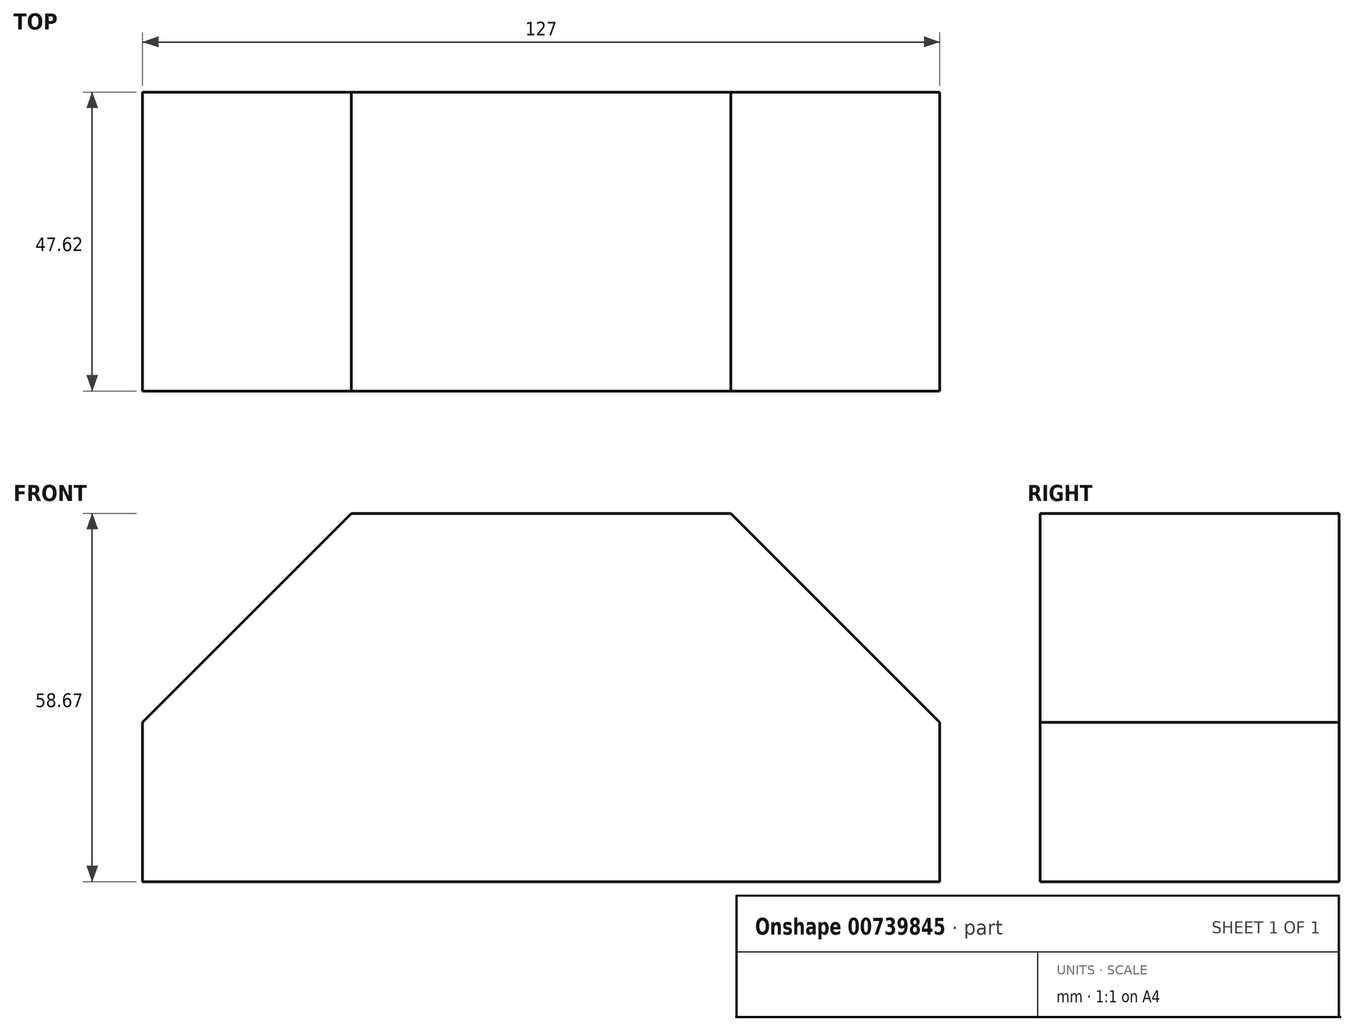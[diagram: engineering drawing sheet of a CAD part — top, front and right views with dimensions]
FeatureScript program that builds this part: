
annotation { "Feature Type Name" : "Feature", "Feature Type Description" : "" }
export const myFeature = defineFeature(function(context is Context, id is Id, definition is map)
    precondition{}
    {
        {
            var Q0;
            Q0=qCreatedBy(makeId("Front.planeOp"),FACE);
            var sketch = newSketch(context, id + "F0", { "sketchPlane" : qUnion([Q0])});
            skLineSegment(sketch, "E0", {"start": v(-62.45, -58.67) * mm, "end": v(64.55, -58.67) * mm});
            skLineSegment(sketch, "E1", {"start": v(64.55, -58.67) * mm, "end": v(64.55, -33.27) * mm});
            skLineSegment(sketch, "E2", {"start": v(64.55, -33.27) * mm, "end": v(31.27, 0) * mm});
            skLineSegment(sketch, "E3", {"start": v(31.27, 0) * mm, "end": v(-29.18, 0) * mm});
            skLineSegment(sketch, "E4", {"start": v(-29.18, 0) * mm, "end": v(-62.45, -33.27) * mm});
            skLineSegment(sketch, "E5", {"start": v(-62.45, -33.27) * mm, "end": v(-62.45, -58.67) * mm});
            skSolve(sketch);
        }
        {
            var Q0;
            Q0 = qSketchRegion(id + "F0", true);
            extrude(context, id + "F1", {"entities" : qUnion([Q0]), "depth" : 47.62 * mm, "offsetDistance" : 25.4 * mm});
        }
    });
